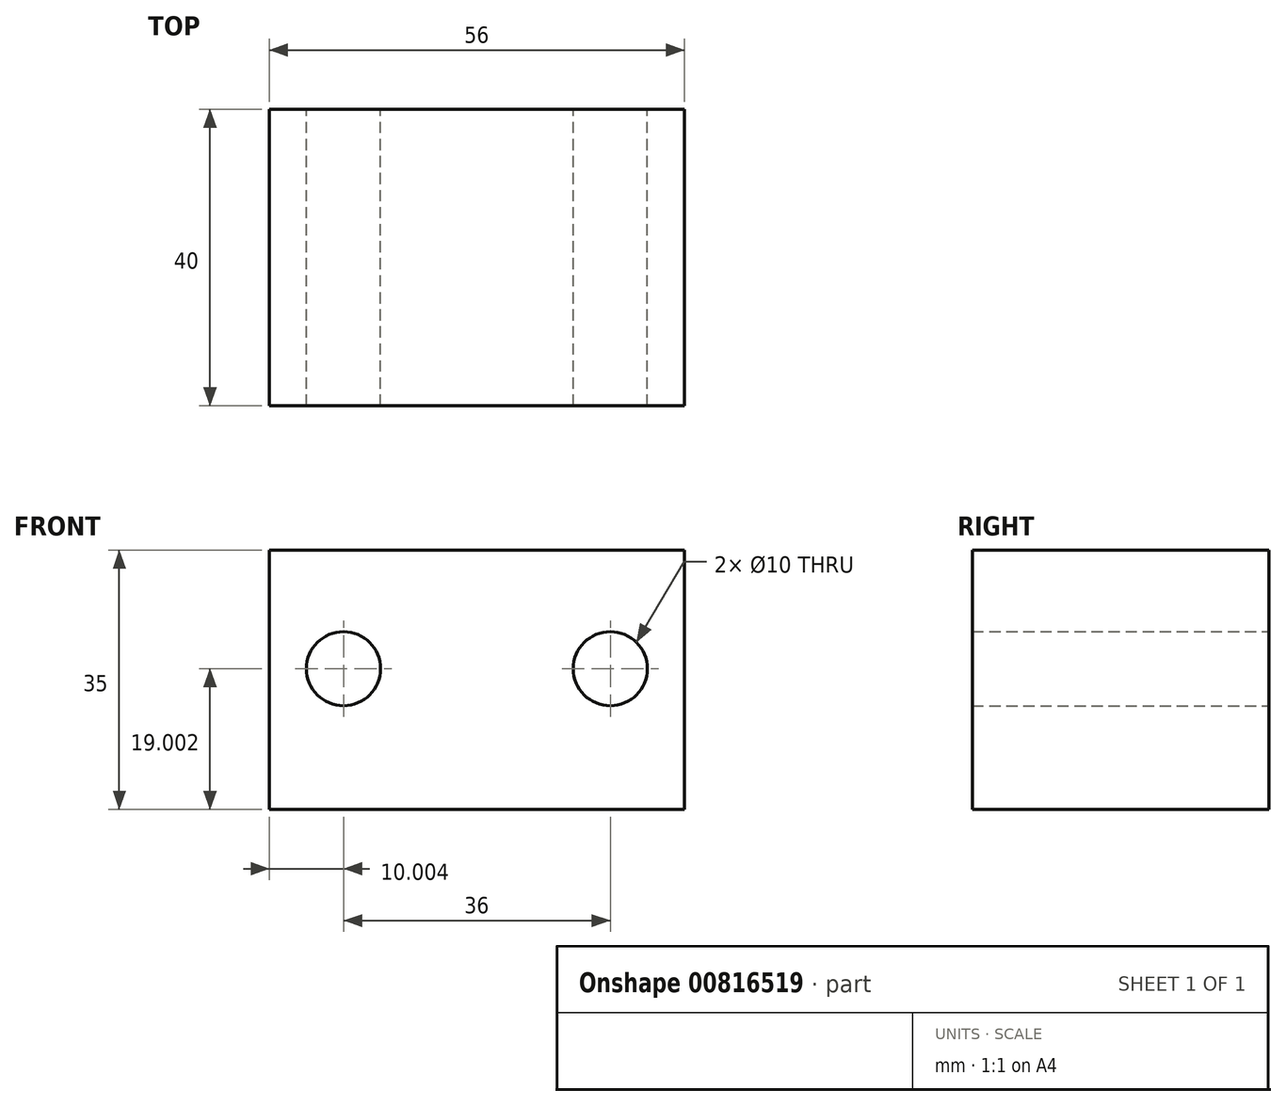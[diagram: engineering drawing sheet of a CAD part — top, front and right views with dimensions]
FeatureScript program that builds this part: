
annotation { "Feature Type Name" : "Feature", "Feature Type Description" : "" }
export const myFeature = defineFeature(function(context is Context, id is Id, definition is map)
    precondition{}
    {
        {
            var Q0;
            Q0=qCreatedBy(makeId("Front.planeOp"),FACE);
            var sketch = newSketch(context, id + "F0", { "sketchPlane" : qUnion([Q0])});
            skLineSegment(sketch, "E0.bottom", {"start": v(-24.3, 12.54) * mm, "end": v(31.7, 12.54) * mm});
            skLineSegment(sketch, "E0.top", {"start": v(-24.3, -22.46) * mm, "end": v(31.7, -22.46) * mm});
            skLineSegment(sketch, "E0.left", {"start": v(-24.3, 12.54) * mm, "end": v(-24.3, -22.46) * mm});
            skLineSegment(sketch, "E0.right", {"start": v(31.7, 12.54) * mm, "end": v(31.7, -22.46) * mm});
            skLineSegment(sketch, "E1", {"start": v(3.7, 12.54) * mm, "end": v(3.7, -38.2) * mm, "construction": true});
            skCircle(sketch, "E2", {"center": v(-14.3, -3.46) * mm, "radius": 5 * mm});
            skCircle(sketch, "E3.MirrorC", {"center": v(21.7, -3.46) * mm, "radius": 5 * mm});
            skSolve(sketch);
        }
        {
            var Q0;
            Q0=makeQuery(id+"F0.imprint","IMPRINT",FACE,{"disambiguationData":[TD([[makeQuery(id+"F0.imprint","IMPRINT",EDGE,{"derivedFrom":sQuery(id+"F0.wireOp",EDGE,"E0.bottom")}),-1.0]])]});
            extrude(context, id + "F1", {"entities" : qUnion([Q0]), "depth" : 40 * mm, "offsetDistance" : 25 * mm});
        }
    });
